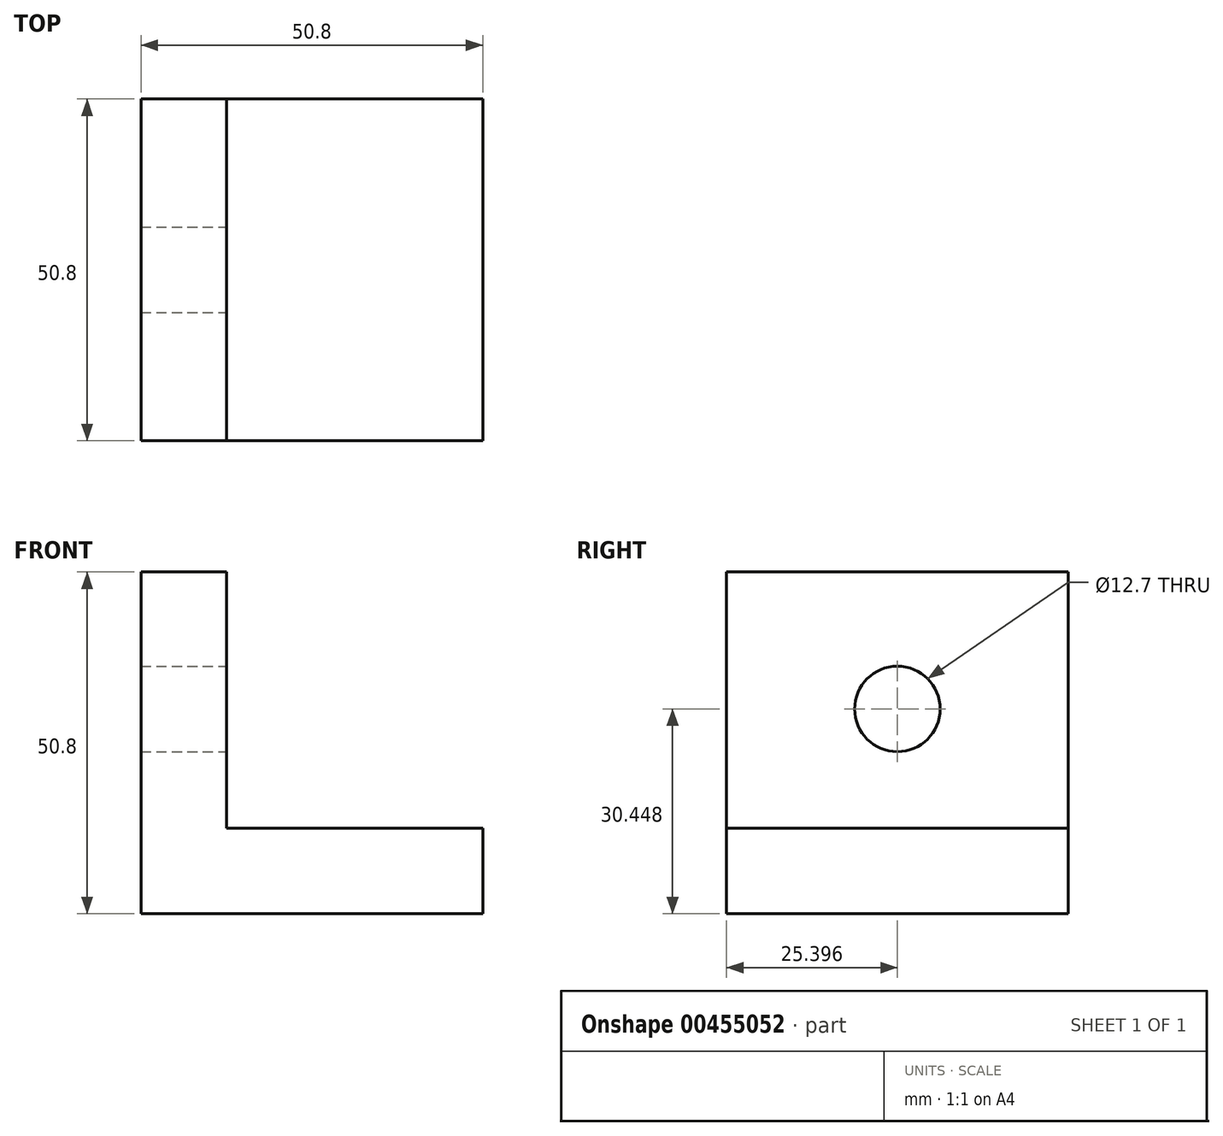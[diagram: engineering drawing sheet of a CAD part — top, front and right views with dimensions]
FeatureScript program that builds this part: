
annotation { "Feature Type Name" : "Feature", "Feature Type Description" : "" }
export const myFeature = defineFeature(function(context is Context, id is Id, definition is map)
    precondition{}
    {
        {
            var Q0;
            Q0=qCreatedBy(makeId("Top.planeOp"),FACE);
            var sketch = newSketch(context, id + "F0", { "sketchPlane" : qUnion([Q0])});
            skLineSegment(sketch, "E0.bottom", {"start": v(-28.4, 13.18) * mm, "end": v(22.4, 13.18) * mm});
            skLineSegment(sketch, "E0.top", {"start": v(-28.4, -37.62) * mm, "end": v(22.4, -37.62) * mm});
            skLineSegment(sketch, "E0.left", {"start": v(-28.4, 13.18) * mm, "end": v(-28.4, -37.62) * mm});
            skLineSegment(sketch, "E0.right", {"start": v(22.4, 13.18) * mm, "end": v(22.4, -37.62) * mm});
            skLineSegment(sketch, "E1", {"start": v(-28.4, 13.18) * mm, "end": v(-15.7, 13.18) * mm});
            skLineSegment(sketch, "E2", {"start": v(-15.7, 13.18) * mm, "end": v(-15.7, -37.62) * mm});
            skSolve(sketch);
        }
        {
            var Q0;
            {var subQ0=sQuery(id+"F0.wireOp",EDGE,"E0.left");Q0=makeQuery(id+"F0.imprint","IMPRINT",FACE,{"disambiguationData":[TD([[makeQuery(id+"F0.imprint","IMPRINT",EDGE,{"derivedFrom":subQ0}),1.0]])]});}
            extrude(context, id + "F1", {"entities" : qUnion([Q0]), "depth" : 50.8 * mm});
        }
        {
            var Q0;
            Q0=makeQuery(id+"F0.imprint","IMPRINT",FACE,{"disambiguationData":[TD([[makeQuery(id+"F0.imprint","IMPRINT",EDGE,{"derivedFrom":sQuery(id+"F0.wireOp",EDGE,"E0.bottom")}),-1.0]])]});
            extrude(context, id + "F2", {"entities" : qUnion([Q0]), "operationType" : NewBodyOperationType.ADD, "depth" : 12.7 * mm});
        }
        {
            var Q0;
            Q0=qCreatedBy(makeId("Right.planeOp"),FACE);
            var sketch = newSketch(context, id + "F3", { "sketchPlane" : qUnion([Q0])});
            skCircle(sketch, "E3", {"center": v(-12.22, 30.45) * mm, "radius": 6.35 * mm});
            skSolve(sketch);
        }
        {
            var Q0;
            Q0=makeQuery(id+"F3.imprint","IMPRINT",FACE,{"disambiguationData":[TD([[makeQuery(id+"F3.imprint","IMPRINT",EDGE,{"derivedFrom":sQuery(id+"F3.wireOp",EDGE,"E3")}),1.0]])]});
            extrude(context, id + "F4", {"entities" : qUnion([Q0]), "operationType" : NewBodyOperationType.REMOVE, "oppositeDirection" : true, "depth" : 49.78 * mm});
        }
    });
